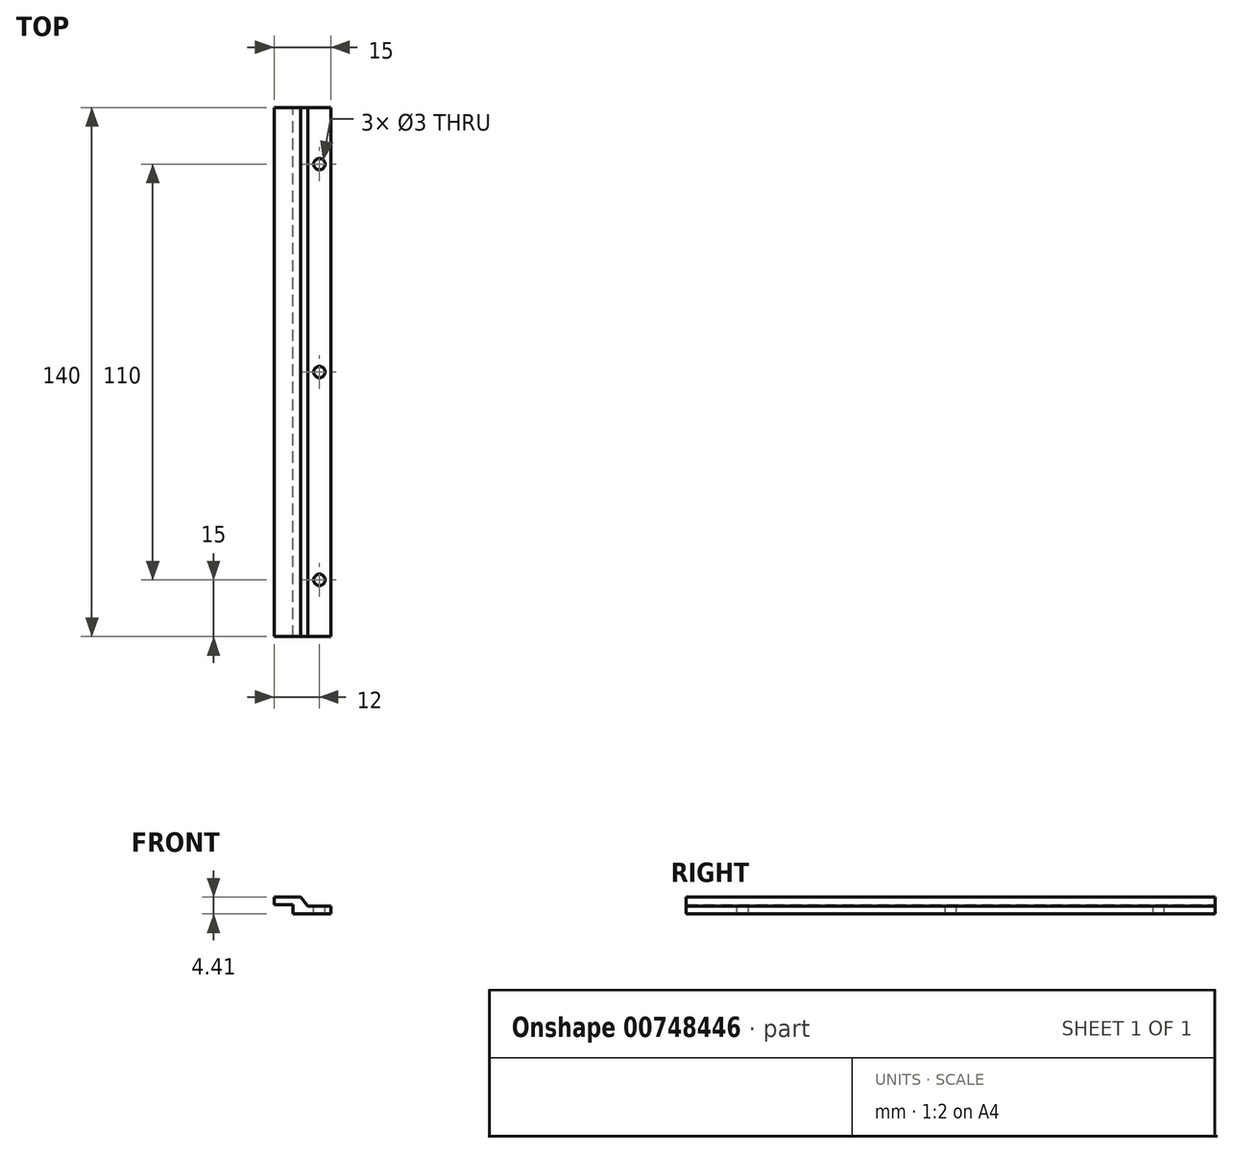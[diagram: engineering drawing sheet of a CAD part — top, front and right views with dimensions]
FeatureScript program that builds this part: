
annotation { "Feature Type Name" : "Feature", "Feature Type Description" : "" }
export const myFeature = defineFeature(function(context is Context, id is Id, definition is map)
    precondition{}
    {
        {
            var Q0;
            Q0=qCreatedBy(makeId("Front.planeOp"),FACE);
            var sketch = newSketch(context, id + "F0", { "sketchPlane" : qUnion([Q0])});
            skLineSegment(sketch, "E0", {"start": v(0, 2.4) * mm, "end": v(0, 4.4) * mm});
            skLineSegment(sketch, "E1", {"start": v(0, 4.4) * mm, "end": v(6.99, 4.4) * mm});
            skLineSegment(sketch, "E2", {"start": v(6.99, 4.4) * mm, "end": v(9, 2) * mm});
            skLineSegment(sketch, "E3", {"start": v(9, 2) * mm, "end": v(15, 2) * mm});
            skLineSegment(sketch, "E4", {"start": v(15, 2) * mm, "end": v(15, 0) * mm});
            skLineSegment(sketch, "E5", {"start": v(15, 0) * mm, "end": v(5, 0) * mm});
            skLineSegment(sketch, "E6", {"start": v(5, 0) * mm, "end": v(5, 2.4) * mm});
            skLineSegment(sketch, "E7", {"start": v(5, 2.4) * mm, "end": v(0, 2.4) * mm});
            skSolve(sketch);
        }
        {
            var Q0;
            Q0=makeQuery(id+"F0.imprint","IMPRINT",FACE,{"disambiguationData":[TD([[makeQuery(id+"F0.imprint","IMPRINT",EDGE,{"derivedFrom":sQuery(id+"F0.wireOp",EDGE,"E0")}),-1.0]])]});
            extrude(context, id + "F1", {"entities" : qUnion([Q0]), "depth" : 140 * mm, "offsetDistance" : 25 * mm});
        }
        {
            var Q0;
            Q0=makeQuery(id+"F1.opExtrude","SWEPT_FACE",FACE,{"disambiguationData":[OSD([sQuery(id+"F0.wireOp",EDGE,"E3")])]});
            var sketch = newSketch(context, id + "F2", { "sketchPlane" : qUnion([Q0])});
            skCircle(sketch, "E8", {"center": v(12, -125) * mm, "radius": 1.5 * mm});
            skLineSegment(sketch, "E9", {"start": v(12, -140) * mm, "end": v(12, -125) * mm, "construction": true});
            skCircle(sketch, "E10", {"center": v(12, -15) * mm, "radius": 1.5 * mm});
            skLineSegment(sketch, "E11", {"start": v(12, 0) * mm, "end": v(12, -15) * mm, "construction": true});
            skLineSegment(sketch, "E12", {"start": v(15, -70) * mm, "end": v(9, -70) * mm, "construction": true});
            skCircle(sketch, "E13", {"center": v(12, -70) * mm, "radius": 1.5 * mm});
            skSolve(sketch);
        }
        {
            var Q0;
            Q0=makeQuery(id+"F2.imprint","IMPRINT",FACE,{"disambiguationData":[TD([[makeQuery(id+"F2.imprint","IMPRINT",EDGE,{"derivedFrom":sQuery(id+"F2.wireOp",EDGE,"E8")}),1.0]])]});
            var Q1;
            Q1=makeQuery(id+"F2.imprint","IMPRINT",FACE,{"disambiguationData":[TD([[makeQuery(id+"F2.imprint","IMPRINT",EDGE,{"derivedFrom":sQuery(id+"F2.wireOp",EDGE,"E13")}),1.0]])]});
            var Q2;
            Q2=makeQuery(id+"F2.imprint","IMPRINT",FACE,{"disambiguationData":[TD([[makeQuery(id+"F2.imprint","IMPRINT",EDGE,{"derivedFrom":sQuery(id+"F2.wireOp",EDGE,"E10")}),1.0]])]});
            extrude(context, id + "F3", {"entities" : qUnion([Q0, Q1, Q2]), "operationType" : NewBodyOperationType.REMOVE, "oppositeDirection" : true, "depth" : 25 * mm, "offsetDistance" : 25 * mm});
        }
    });
